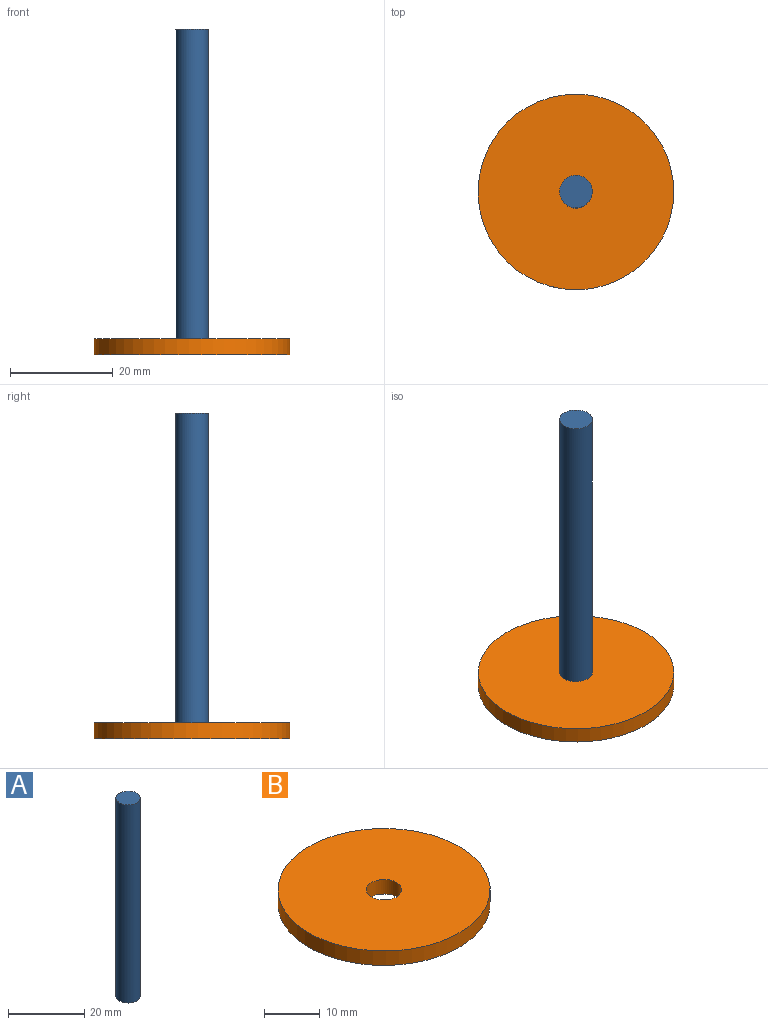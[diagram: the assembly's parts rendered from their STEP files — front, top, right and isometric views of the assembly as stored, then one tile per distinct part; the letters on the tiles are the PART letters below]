
ASSEMBLY  parts=2 mates=1
PART A: 3 faces, bbox 6.4x6.4x63.5 mm
  f0: plane 6.35x6.35mm, normal (0,0,1), area 31.7mm2, adj f1
  f1: cylinder r=3.17mm len=63.5mm, axis (0,0,-1), area 1266.8mm2, adj f0,f2
  f2: plane 6.35x6.35mm, normal (0,0,-1), area 31.7mm2, adj f1
PART B: 4 faces, bbox 38.1x38.1x3.2 mm
  f0: cylinder r=3.17mm len=6.35mm, axis (0,0,-1), area 63.3mm2, adj f2,f3
  f1: cylinder r=19.05mm len=38.1mm, axis (0,0,-1), area 380mm2, adj f2,f3
  f2: plane 38.1x38.1mm, normal (0,0,1), area 1108.4mm2, adj f0,f1
  f3: plane 38.1x38.1mm, normal (0,0,-1), area 1108.4mm2, adj f0,f1
PLACE A t=(-69.85,0,-69.85)mm
PLACE B t=(-69.85,0,-69.85)mm
MATE fastened B.f0 <-> A.f1  axis (0,0,-1) through (0,0,0)mm
